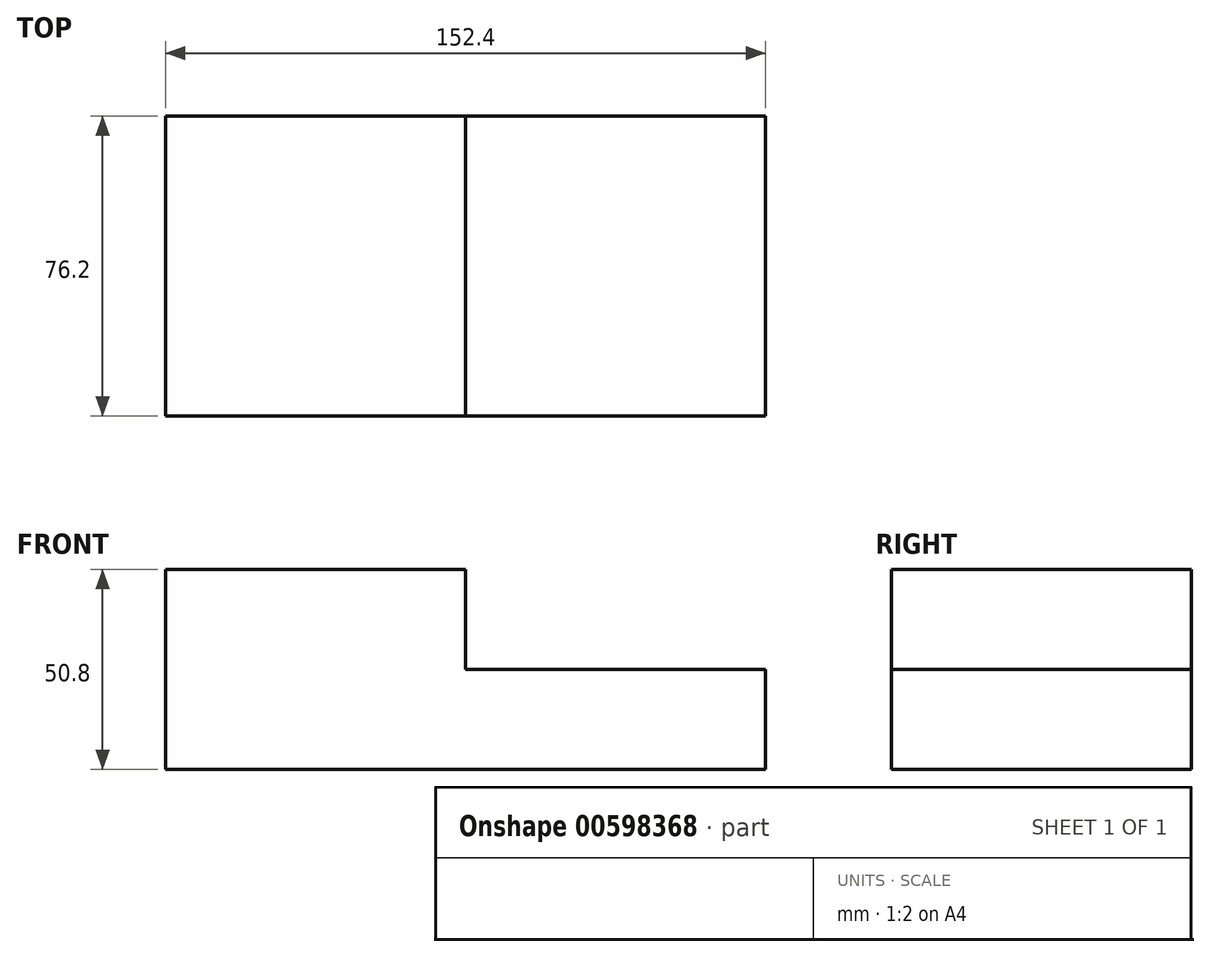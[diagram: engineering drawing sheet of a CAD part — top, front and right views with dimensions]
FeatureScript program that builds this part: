
annotation { "Feature Type Name" : "Feature", "Feature Type Description" : "" }
export const myFeature = defineFeature(function(context is Context, id is Id, definition is map)
    precondition{}
    {
        {
            var Q0;
            Q0=qCreatedBy(makeId("Front.planeOp"),FACE);
            var sketch = newSketch(context, id + "F0", { "sketchPlane" : qUnion([Q0])});
            skLineSegment(sketch, "E0", {"start": v(0, 0) * mm, "end": v(0, 50.8) * mm});
            skLineSegment(sketch, "E1", {"start": v(76.2, 50.8) * mm, "end": v(0, 50.8) * mm});
            skLineSegment(sketch, "E2", {"start": v(76.2, 50.8) * mm, "end": v(76.2, 25.4) * mm});
            skLineSegment(sketch, "E3", {"start": v(76.2, 25.4) * mm, "end": v(152.4, 25.4) * mm});
            skLineSegment(sketch, "E4", {"start": v(152.4, 25.4) * mm, "end": v(152.4, 0) * mm});
            skLineSegment(sketch, "E5", {"start": v(152.4, 0) * mm, "end": v(0, 0) * mm});
            skSolve(sketch);
        }
        {
            var Q0;
            Q0 = qSketchRegion(id + "F0", true);
            extrude(context, id + "F1", {"entities" : qUnion([Q0]), "depth" : 76.2 * mm, "offsetDistance" : 25.4 * mm});
        }
    });
